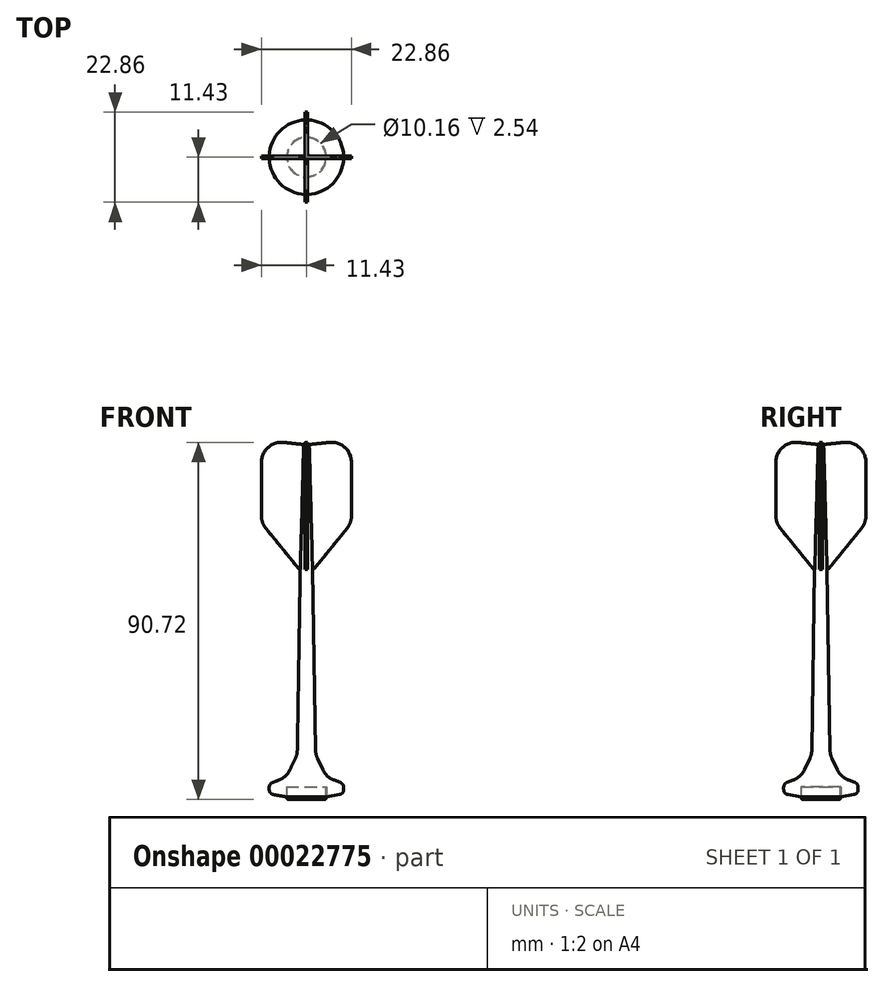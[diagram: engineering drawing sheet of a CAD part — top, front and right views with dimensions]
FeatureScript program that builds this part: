
annotation { "Feature Type Name" : "Feature", "Feature Type Description" : "" }
export const myFeature = defineFeature(function(context is Context, id is Id, definition is map)
    precondition{}
    {
        {
            var Q0;
            Q0=qCreatedBy(makeId("Front.planeOp"),FACE);
            var sketch = newSketch(context, id + "F0", { "sketchPlane" : qUnion([Q0])});
            skLineSegment(sketch, "E0", {"start": v(-1.59, 54.42) * mm, "end": v(-2.34, 7.43) * mm});
            skLineSegment(sketch, "E1", {"start": v(-2.34, 7.43) * mm, "end": v(-5.08, 1.7) * mm});
            skLineSegment(sketch, "E2", {"start": v(-5.08, 1.7) * mm, "end": v(-9.46, 0) * mm});
            skLineSegment(sketch, "E3", {"start": v(-9.46, 0) * mm, "end": v(-9.46, -2.54) * mm});
            skLineSegment(sketch, "E4", {"start": v(-9.46, -2.54) * mm, "end": v(-5.08, -3.3) * mm});
            skLineSegment(sketch, "E5", {"start": v(0, -3.3) * mm, "end": v(0, 0) * mm});
            skLineSegment(sketch, "E6", {"start": v(-1.59, 54.42) * mm, "end": v(-0.76, 86.15) * mm});
            skLineSegment(sketch, "E7", {"start": v(-0.76, 86.15) * mm, "end": v(0, 86.15) * mm});
            skLineSegment(sketch, "E8", {"start": v(0, 0) * mm, "end": v(0, 86.15) * mm});
            skLineSegment(sketch, "E9", {"start": v(-5.08, -3.3) * mm, "end": v(-5.08, -0.76) * mm});
            skLineSegment(sketch, "E10", {"start": v(-5.08, -0.76) * mm, "end": v(0, -0.76) * mm});
            skSolve(sketch);
        }
        {
            var Q0;
            Q0=qCreatedBy(makeId("Front.planeOp"),FACE);
            var sketch = newSketch(context, id + "F1", { "sketchPlane" : qUnion([Q0])});
            skLineSegment(sketch, "E11", {"start": v(0, 54.45) * mm, "end": v(0, 86.14) * mm});
            skLineSegment(sketch, "E12", {"start": v(-11.43, 87.35) * mm, "end": v(-11.43, 66.27) * mm});
            skLineSegment(sketch, "E13", {"start": v(-11.43, 66.27) * mm, "end": v(-1.81, 54.45) * mm});
            skLineSegment(sketch, "E14", {"start": v(-1.81, 54.45) * mm, "end": v(0, 54.45) * mm});
            skLineSegment(sketch, "E15", {"start": v(0, 86.14) * mm, "end": v(-11.43, 87.35) * mm});
            skPoint(sketch, "E16", {"position": v(0, 87.35) * mm});
            skSolve(sketch);
        }
        {
            var Q0;
            Q0 = qSketchRegion(id + "F1", true);
            var Q1;
            Q1=sQuery(id+"F1.wireOp",EDGE,"E11");
            revolve(context, id + "F2", {"entities" : qUnion([Q0]), "axis" : qUnion([Q1]), "revolveType" : RevolveType.FULL});
        }
        {
            var Q0;
            Q0=makeQuery(id+"F2.opRevolve","SWEPT_EDGE",EDGE,{"disambiguationData":[OSD([sQuery(id+"F1.wireOp",EDGE,"E12"),sQuery(id+"F1.wireOp",EDGE,"E15")])]});
            var Q1;
            Q1=makeQuery(id+"F2.opRevolve","SWEPT_EDGE",EDGE,{"disambiguationData":[OSD([sQuery(id+"F1.wireOp",EDGE,"E12"),sQuery(id+"F1.wireOp",EDGE,"E13")])]});
            fillet(context, id + "F3", {"entities" : qUnion([Q0, Q1]), "radius" : 5.08 * mm, "tangentPropagation" : true, "allowEdgeOverflow" : false});
        }
        {
            var Q0;
            Q0=makeQuery(id+"F2.opRevolve","SWEPT_EDGE",EDGE,{"disambiguationData":[OSD([sQuery(id+"F1.wireOp",EDGE,"E13"),sQuery(id+"F1.wireOp",EDGE,"E14")])]});
            fillet(context, id + "F4", {"entities" : qUnion([Q0]), "radius" : 0.76 * mm, "allowEdgeOverflow" : false});
        }
        {
            var Q0;
            Q0=makeQuery(id+"F2.opRevolve","SWEPT_FACE",FACE,{"disambiguationData":[OSD([sQuery(id+"F1.wireOp",EDGE,"E14")])]});
            var sketch = newSketch(context, id + "F5", { "sketchPlane" : qUnion([Q0])});
            skLineSegment(sketch, "E17.bottom", {"start": v(-13.02, 0.33) * mm, "end": v(-0.32, 0.33) * mm});
            skLineSegment(sketch, "E17.top", {"start": v(-13.02, 13.03) * mm, "end": v(-0.32, 13.03) * mm});
            skLineSegment(sketch, "E17.left", {"start": v(-13.02, 0.33) * mm, "end": v(-13.02, 13.03) * mm});
            skLineSegment(sketch, "E17.right", {"start": v(-0.32, 0.33) * mm, "end": v(-0.32, 13.03) * mm});
            skLineSegment(sketch, "E18.1.0", {"start": v(-13.03, -13.02) * mm, "end": v(-13.03, -0.32) * mm});
            skLineSegment(sketch, "E18.1.1", {"start": v(-0.33, -0.32) * mm, "end": v(-13.03, -0.32) * mm});
            skLineSegment(sketch, "E18.1.2", {"start": v(-0.33, -0.32) * mm, "end": v(-0.33, -13.02) * mm});
            skLineSegment(sketch, "E18.1.3", {"start": v(-0.33, -13.02) * mm, "end": v(-13.03, -13.02) * mm});
            skLineSegment(sketch, "E18.2.0", {"start": v(13.02, -13.03) * mm, "end": v(0.32, -13.03) * mm});
            skLineSegment(sketch, "E18.2.1", {"start": v(0.32, -0.33) * mm, "end": v(0.32, -13.03) * mm});
            skLineSegment(sketch, "E18.2.2", {"start": v(0.32, -0.33) * mm, "end": v(13.02, -0.33) * mm});
            skLineSegment(sketch, "E18.2.3", {"start": v(13.02, -0.33) * mm, "end": v(13.02, -13.03) * mm});
            skLineSegment(sketch, "E18.3.0", {"start": v(13.03, 13.02) * mm, "end": v(13.03, 0.32) * mm});
            skLineSegment(sketch, "E18.3.1", {"start": v(0.33, 0.32) * mm, "end": v(13.03, 0.32) * mm});
            skLineSegment(sketch, "E18.3.2", {"start": v(0.33, 0.32) * mm, "end": v(0.33, 13.02) * mm});
            skLineSegment(sketch, "E18.3.3", {"start": v(0.33, 13.02) * mm, "end": v(13.03, 13.02) * mm});
            skPoint(sketch, "E18.center", {"position": v(0, 0) * mm});
            skSolve(sketch);
        }
        {
            var Q0;
            Q0 = qSketchRegion(id + "F5", true);
            extrude(context, id + "F6", {"entities" : qUnion([Q0]), "operationType" : NewBodyOperationType.REMOVE, "endBound" : BoundingType.THROUGH_ALL, "oppositeDirection" : true, "depth" : 25.4 * mm});
        }
        {
            var Q0;
            Q0=makeQuery(id+"F0.imprint","IMPRINT",FACE,{"disambiguationData":[TD([[makeQuery(id+"F0.imprint","IMPRINT",EDGE,{"derivedFrom":sQuery(id+"F0.wireOp",EDGE,"E0")}),1.0]])]});
            var Q1;
            Q1=sQuery(id+"F0.wireOp",EDGE,"E8");
            revolve(context, id + "F7", {"operationType" : NewBodyOperationType.ADD, "entities" : qUnion([Q0]), "axis" : qUnion([Q1]), "revolveType" : RevolveType.FULL});
        }
        {
            var Q0;
            Q0=makeQuery(id+"F7.opRevolve","SWEPT_EDGE",EDGE,{"disambiguationData":[OSD([sQuery(id+"F0.wireOp",EDGE,"E3"),sQuery(id+"F0.wireOp",EDGE,"E4")])]});
            var Q1;
            Q1=makeQuery(id+"F7.opRevolve","SWEPT_EDGE",EDGE,{"disambiguationData":[OSD([sQuery(id+"F0.wireOp",EDGE,"E2"),sQuery(id+"F0.wireOp",EDGE,"E3")])]});
            fillet(context, id + "F8", {"entities" : qUnion([Q0, Q1]), "radius" : 1.27 * mm, "tangentPropagation" : true, "allowEdgeOverflow" : false});
        }
        {
            var Q0;
            Q0=makeQuery(id+"F7.opRevolve","SWEPT_EDGE",EDGE,{"disambiguationData":[OSD([sQuery(id+"F0.wireOp",EDGE,"E1"),sQuery(id+"F0.wireOp",EDGE,"E2")])]});
            var Q1;
            Q1=makeQuery(id+"F7.opRevolve","SWEPT_EDGE",EDGE,{"disambiguationData":[OSD([sQuery(id+"F0.wireOp",EDGE,"E0"),sQuery(id+"F0.wireOp",EDGE,"E1")])]});
            fillet(context, id + "F9", {"entities" : qUnion([Q0, Q1]), "radius" : 5.08 * mm, "tangentPropagation" : true, "allowEdgeOverflow" : false});
        }
        {
            var Q0;
            Q0=makeQuery(id+"F7.opRevolve","SWEPT_FACE",FACE,{"disambiguationData":[OSD([sQuery(id+"F0.wireOp",EDGE,"E10")])]});
            var sketch = newSketch(context, id + "F10", { "sketchPlane" : qUnion([Q0])});
            skCircle(sketch, "E19", {"center": v(0, 0) * mm, "radius": 4.95 * mm});
            skSolve(sketch);
        }
        {
            var Q0;
            Q0 = qSketchRegion(id + "F10", true);
            extrude(context, id + "F11", {"entities" : qUnion([Q0]), "depth" : 3.17 * mm});
        }
        {
            var Q0;
            Q0=makeQuery(id+"F11.opExtrude","CAP_EDGE",EDGE,{"disambiguationData":[OSD([sQuery(id+"F10.wireOp",EDGE,"E19")])],"isStart":false});
            fillet(context, id + "F12", {"entities" : qUnion([Q0]), "radius" : 0.25 * mm, "tangentPropagation" : true, "allowEdgeOverflow" : false});
        }
    });
